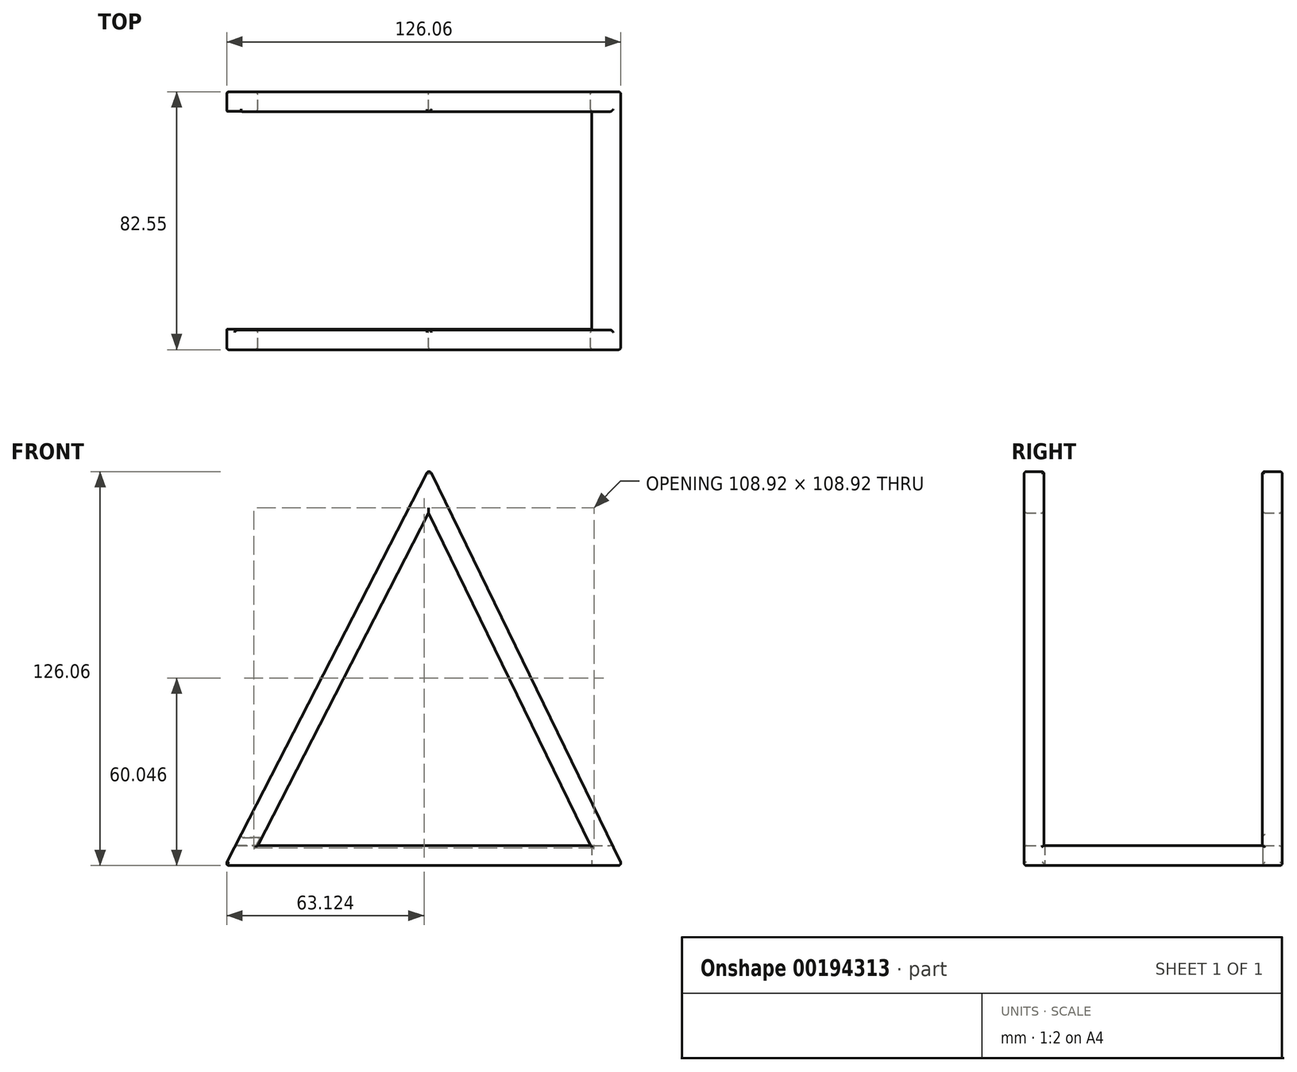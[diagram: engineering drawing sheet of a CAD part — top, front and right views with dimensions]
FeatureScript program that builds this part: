
annotation { "Feature Type Name" : "Feature", "Feature Type Description" : "" }
export const myFeature = defineFeature(function(context is Context, id is Id, definition is map)
    precondition{}
    {
        {
            var Q0;
            Q0=qCreatedBy(makeId("Front.planeOp"),FACE);
            var sketch = newSketch(context, id + "F0", { "sketchPlane" : qUnion([Q0])});
            skLineSegment(sketch, "E0", {"start": v(-65.24, 0) * mm, "end": v(61.76, 0) * mm});
            skLineSegment(sketch, "E1", {"start": v(-65.24, 0) * mm, "end": v(0, 127) * mm});
            skLineSegment(sketch, "E2", {"start": v(0, 127) * mm, "end": v(61.76, 0) * mm});
            skSolve(sketch);
        }
        {
            var Q0;
            Q0=makeQuery(id+"F0.imprint","IMPRINT",FACE,{"disambiguationData":[TD([[makeQuery(id+"F0.imprint","IMPRINT",EDGE,{"derivedFrom":sQuery(id+"F0.wireOp",EDGE,"E0")}),1.0]])]});
            var sketch = newSketch(context, id + "F1", { "sketchPlane" : qUnion([Q0])});
            skLineSegment(sketch, "E3.0", {"start": v(-0.16, 112.8) * mm, "end": v(-54.84, 6.35) * mm});
            skLineSegment(sketch, "E3.1", {"start": v(51.61, 6.35) * mm, "end": v(-0.16, 112.8) * mm});
            skLineSegment(sketch, "E3.2", {"start": v(-54.84, 6.35) * mm, "end": v(51.61, 6.35) * mm});
            skSolve(sketch);
        }
        {
            var Q0;
            Q0=makeQuery(id+"F1.imprint","IMPRINT",FACE,{"disambiguationData":[TD([[makeQuery(id+"F1.imprint","IMPRINT",EDGE,{"derivedFrom":sQuery(id+"F1.wireOp",EDGE,"E3.0")}),-1.0]])]});
            extrude(context, id + "F2", {"entities" : qUnion([Q0]), "depth" : 82.55 * mm});
        }
        {
            var Q0;
            Q0=qCreatedBy(makeId("Right.planeOp"),FACE);
            var sketch = newSketch(context, id + "F3", { "sketchPlane" : qUnion([Q0])});
            skLineSegment(sketch, "E4.bottom", {"start": v(-76.2, 127) * mm, "end": v(-6.35, 127) * mm});
            skLineSegment(sketch, "E4.top", {"start": v(-76.2, 6.35) * mm, "end": v(-6.35, 6.35) * mm});
            skLineSegment(sketch, "E4.left", {"start": v(-76.2, 127) * mm, "end": v(-76.2, 6.35) * mm});
            skLineSegment(sketch, "E4.right", {"start": v(-6.35, 127) * mm, "end": v(-6.35, 6.35) * mm});
            skSolve(sketch);
        }
        {
            var Q0;
            Q0=makeQuery(id+"F3.imprint","IMPRINT",FACE,{"disambiguationData":[TD([[makeQuery(id+"F3.imprint","IMPRINT",EDGE,{"derivedFrom":sQuery(id+"F3.wireOp",EDGE,"E4.bottom")}),-1.0]])]});
            extrude(context, id + "F4", {"entities" : qUnion([Q0]), "operationType" : NewBodyOperationType.REMOVE, "endBound" : BoundingType.SYMMETRIC, "oppositeDirection" : true, "depth" : 254 * mm});
        }
        {
            var Q0;
            Q0=qCreatedBy(makeId("Right.planeOp"),FACE);
            var sketch = newSketch(context, id + "F5", { "sketchPlane" : qUnion([Q0])});
            skLineSegment(sketch, "E5.bottom", {"start": v(-75.94, 8.95) * mm, "end": v(-6.3, 8.95) * mm});
            skLineSegment(sketch, "E5.top", {"start": v(-75.94, -6.63) * mm, "end": v(-6.3, -6.63) * mm});
            skLineSegment(sketch, "E5.left", {"start": v(-75.94, 8.95) * mm, "end": v(-75.94, -6.63) * mm});
            skLineSegment(sketch, "E5.right", {"start": v(-6.3, 8.95) * mm, "end": v(-6.3, -6.63) * mm});
            skSolve(sketch);
        }
        {
            var Q0;
            Q0=makeQuery(id+"F5.imprint","IMPRINT",FACE,{"disambiguationData":[TD([[makeQuery(id+"F5.imprint","IMPRINT",EDGE,{"derivedFrom":sQuery(id+"F5.wireOp",EDGE,"E5.bottom")}),-1.0]])]});
            extrude(context, id + "F6", {"entities" : qUnion([Q0]), "operationType" : NewBodyOperationType.REMOVE, "endBound" : BoundingType.UP_TO_NEXT, "oppositeDirection" : true, "depth" : 127 * mm});
        }
        {
            var Q0;
            Q0=makeQuery(id+"F6.boolean.opBoolean","COPY",FACE,{"derivedFrom":makeQuery(id+"F6.opExtrude","CAP_FACE",FACE,{"disambiguationData":[OSD([sQuery(id+"F5.wireOp",EDGE,"E5.bottom"),sQuery(id+"F5.wireOp",EDGE,"E5.top"),sQuery(id+"F5.wireOp",EDGE,"E5.left"),sQuery(id+"F5.wireOp",EDGE,"E5.right")])],"isStart":true})});
            extrude(context, id + "F7", {"entities" : qUnion([Q0]), "operationType" : NewBodyOperationType.REMOVE, "oppositeDirection" : true, "depth" : 52.07 * mm});
        }
        {
            var Q0;
            Q0=makeQuery(id+"F2.opExtrude","SWEPT_FACE",FACE,{"disambiguationData":[OSD([sQuery(id+"F0.wireOp",EDGE,"E2")])]});
            var Q1;
            Q1=makeQuery(id+"F2.opExtrude","CAP_FACE",FACE,{"disambiguationData":[OSD([sQuery(id+"F0.wireOp",EDGE,"E0"),sQuery(id+"F0.wireOp",EDGE,"E1"),sQuery(id+"F0.wireOp",EDGE,"E2"),sQuery(id+"F1.wireOp",EDGE,"E3.0"),sQuery(id+"F1.wireOp",EDGE,"E3.1"),sQuery(id+"F1.wireOp",EDGE,"E3.2")])],"isStart":false});
            var Q2;
            Q2=makeQuery(id+"F2.opExtrude","CAP_FACE",FACE,{"disambiguationData":[OSD([sQuery(id+"F0.wireOp",EDGE,"E0"),sQuery(id+"F0.wireOp",EDGE,"E1"),sQuery(id+"F0.wireOp",EDGE,"E2"),sQuery(id+"F1.wireOp",EDGE,"E3.0"),sQuery(id+"F1.wireOp",EDGE,"E3.1"),sQuery(id+"F1.wireOp",EDGE,"E3.2")])],"isStart":true});
            fillet(context, id + "F8", {"entities" : qUnion([Q0, Q1, Q2]), "radius" : 0.76 * mm, "tangentPropagation" : true, "allowEdgeOverflow" : false});
        }
        {
            var Q0;
            {var subQ2=sQuery(id+"F0.wireOp",EDGE,"E1");Q0=makeQuery(id+"F6.boolean.opBoolean","SPLIT",FACE,{"disambiguationData":[TD([makeQuery(id+"F4.boolean.opBoolean","COPY",FACE,{"derivedFrom":makeQuery(id+"F4.opExtrude","SWEPT_FACE",FACE,{"disambiguationData":[OSD([sQuery(id+"F3.wireOp",EDGE,"E4.right")])]})})])],"derivedFrom":makeQuery(id+"F2.opExtrude","SWEPT_FACE",FACE,{"disambiguationData":[OSD([subQ2])]})});}
            var Q1;
            {var subQ1=sQuery(id+"F1.wireOp",EDGE,"E3.2");var subQ3=sQuery(id+"F0.wireOp",EDGE,"E1");Q1=makeQuery(id+"F6.boolean.opBoolean","SPLIT",FACE,{"disambiguationData":[TD([makeQuery(id+"F2.opExtrude","SWEPT_FACE",FACE,{"disambiguationData":[OSD([subQ1])]})])],"derivedFrom":makeQuery(id+"F2.opExtrude","SWEPT_FACE",FACE,{"disambiguationData":[OSD([subQ3])]})});}
            fillet(context, id + "F9", {"entities" : qUnion([Q0, Q1]), "radius" : 0.76 * mm, "tangentPropagation" : true, "allowEdgeOverflow" : false});
        }
        {
            var Q0;
            Q0=makeQuery(id+"F4.boolean.opBoolean","INTERSECT",EDGE,{"derivedFrom":[makeQuery(id+"F2.opExtrude","SWEPT_FACE",FACE,{"disambiguationData":[OSD([sQuery(id+"F1.wireOp",EDGE,"E3.1")])]}),makeQuery(id+"F4.opExtrude","SWEPT_FACE",FACE,{"disambiguationData":[OSD([sQuery(id+"F3.wireOp",EDGE,"E4.left")])]})]});
            var Q1;
            Q1=makeQuery(id+"F4.boolean.opBoolean","INTERSECT",EDGE,{"derivedFrom":[makeQuery(id+"F2.opExtrude","SWEPT_FACE",FACE,{"disambiguationData":[OSD([sQuery(id+"F1.wireOp",EDGE,"E3.1")])]}),makeQuery(id+"F4.opExtrude","SWEPT_FACE",FACE,{"disambiguationData":[OSD([sQuery(id+"F3.wireOp",EDGE,"E4.right")])]})]});
            var Q2;
            Q2=makeQuery(id+"F4.boolean.opBoolean","INTERSECT",EDGE,{"derivedFrom":[makeQuery(id+"F2.opExtrude","SWEPT_FACE",FACE,{"disambiguationData":[OSD([sQuery(id+"F1.wireOp",EDGE,"E3.0")])]}),makeQuery(id+"F4.opExtrude","SWEPT_FACE",FACE,{"disambiguationData":[OSD([sQuery(id+"F3.wireOp",EDGE,"E4.left")])]})]});
            var Q3;
            Q3=makeQuery(id+"F4.boolean.opBoolean","INTERSECT",EDGE,{"derivedFrom":[makeQuery(id+"F2.opExtrude","SWEPT_FACE",FACE,{"disambiguationData":[OSD([sQuery(id+"F1.wireOp",EDGE,"E3.0")])]}),makeQuery(id+"F4.opExtrude","SWEPT_FACE",FACE,{"disambiguationData":[OSD([sQuery(id+"F3.wireOp",EDGE,"E4.right")])]})]});
            fillet(context, id + "F10", {"entities" : qUnion([Q0, Q1, Q2, Q3]), "radius" : 0.76 * mm, "tangentPropagation" : true, "allowEdgeOverflow" : false});
        }
    });
